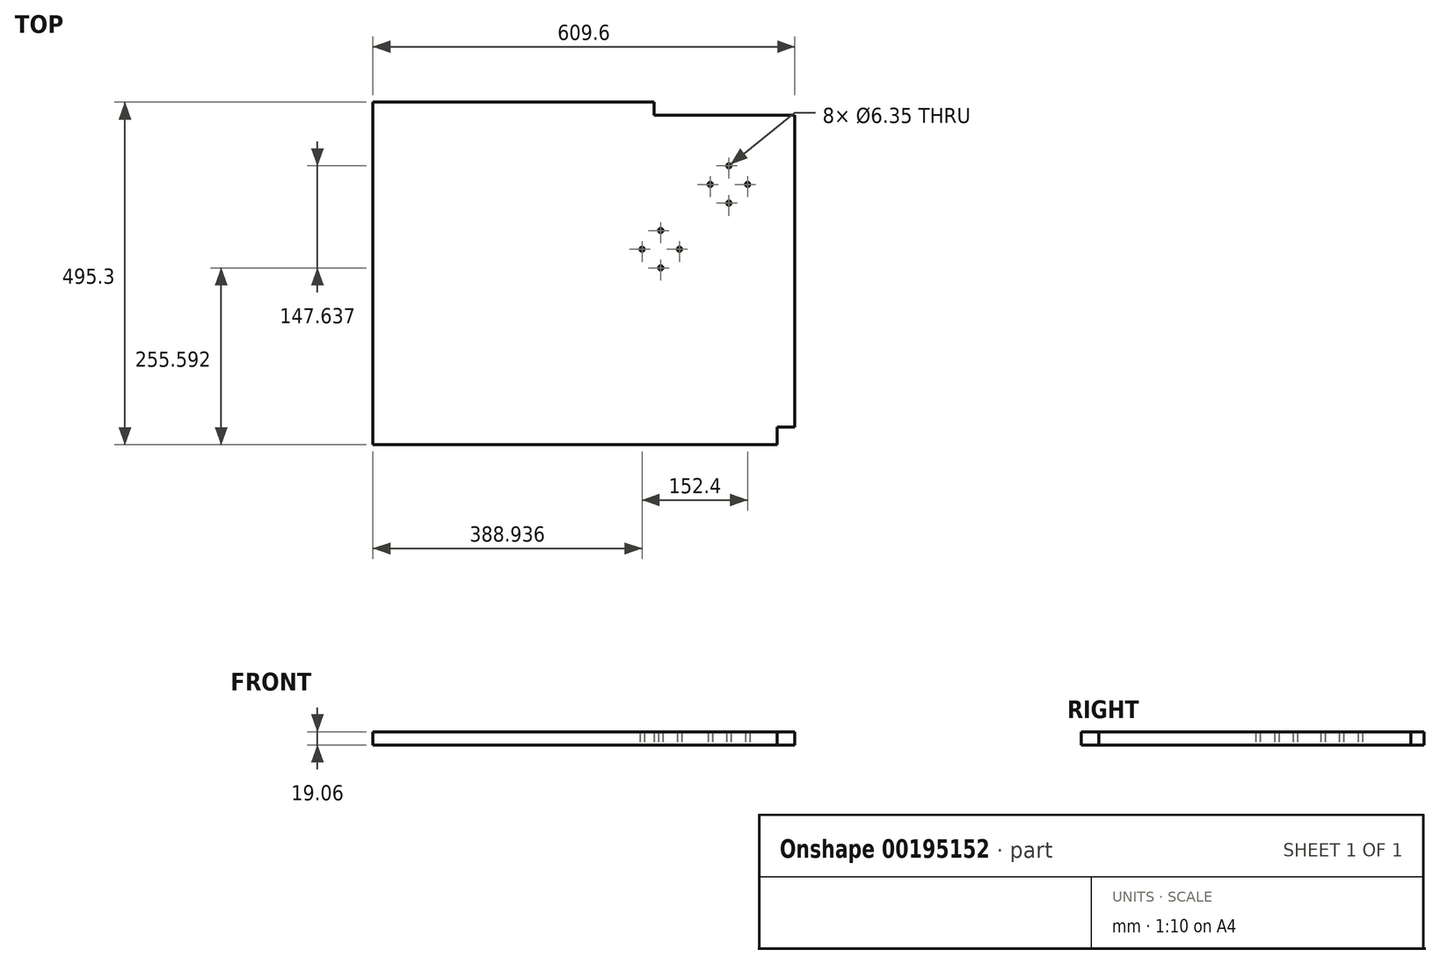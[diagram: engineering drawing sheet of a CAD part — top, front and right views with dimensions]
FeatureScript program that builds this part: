
annotation { "Feature Type Name" : "Feature", "Feature Type Description" : "" }
export const myFeature = defineFeature(function(context is Context, id is Id, definition is map)
    precondition{}
    {
        {
            var Q0;
            Q0=qCreatedBy(makeId("Top.planeOp"),FACE);
            var sketch = newSketch(context, id + "F0", { "sketchPlane" : qUnion([Q0])});
            skLineSegment(sketch, "E0", {"start": v(-565.53, 243.12) * mm, "end": v(-565.53, -252.18) * mm});
            skLineSegment(sketch, "E1", {"start": v(-565.53, -252.18) * mm, "end": v(18.67, -252.18) * mm});
            skLineSegment(sketch, "E2", {"start": v(18.67, -252.18) * mm, "end": v(18.67, -226.78) * mm});
            skLineSegment(sketch, "E3", {"start": v(18.67, -226.78) * mm, "end": v(44.07, -226.78) * mm});
            skLineSegment(sketch, "E4", {"start": v(44.07, -226.78) * mm, "end": v(44.07, 224.07) * mm});
            skLineSegment(sketch, "E5", {"start": v(44.07, 224.07) * mm, "end": v(-159.13, 224.07) * mm});
            skLineSegment(sketch, "E6", {"start": v(-159.13, 224.07) * mm, "end": v(-159.13, 243.12) * mm});
            skLineSegment(sketch, "E7", {"start": v(-159.13, 243.12) * mm, "end": v(-565.53, 243.12) * mm});
            skLineSegment(sketch, "E8", {"start": v(-418.3, -252.18) * mm, "end": v(-418.3, 30.4) * mm, "construction": true});
            skLineSegment(sketch, "E9", {"start": v(-273.43, -252.18) * mm, "end": v(-273.43, 124.06) * mm, "construction": true});
            skLineSegment(sketch, "E10", {"start": v(-273.43, 124.06) * mm, "end": v(44.07, 124.06) * mm, "construction": true});
            skLineSegment(sketch, "E11", {"start": v(-418.3, 30.4) * mm, "end": v(44.07, 30.4) * mm, "construction": true});
            skLineSegment(sketch, "E12", {"start": v(44.07, 178.98) * mm, "end": v(-51.18, 178.98) * mm, "construction": true});
            skLineSegment(sketch, "E13", {"start": v(-51.18, 178.98) * mm, "end": v(-51.18, -252.18) * mm, "construction": true});
            skLineSegment(sketch, "E14", {"start": v(44.07, 204.94) * mm, "end": v(-149.6, 204.94) * mm, "construction": true});
            skLineSegment(sketch, "E15", {"start": v(-149.6, 204.94) * mm, "end": v(-149.6, -252.18) * mm, "construction": true});
            skPoint(sketch, "E16", {"position": v(-149.6, 30.4) * mm});
            skPoint(sketch, "E17", {"position": v(-51.18, 124.06) * mm});
            skCircle(sketch, "E18", {"center": v(-149.6, 30.4) * mm, "radius": 26.99 * mm, "construction": true});
            skCircle(sketch, "E19", {"center": v(-51.18, 124.06) * mm, "radius": 26.99 * mm, "construction": true});
            skPoint(sketch, "E20", {"position": v(-149.6, 3.41) * mm});
            skPoint(sketch, "E21", {"position": v(-51.18, 97.07) * mm});
            skPoint(sketch, "E22", {"position": v(-24.2, 124.06) * mm});
            skPoint(sketch, "E23", {"position": v(-51.18, 151.05) * mm});
            skPoint(sketch, "E24", {"position": v(-78.17, 124.06) * mm});
            skPoint(sketch, "E25", {"position": v(-149.6, 57.39) * mm});
            skPoint(sketch, "E26", {"position": v(-176.6, 30.4) * mm});
            skPoint(sketch, "E27", {"position": v(-122.62, 30.4) * mm});
            skCircle(sketch, "E28", {"center": v(-149.6, 57.39) * mm, "radius": 3.18 * mm});
            skCircle(sketch, "E29", {"center": v(-176.6, 30.4) * mm, "radius": 3.18 * mm});
            skCircle(sketch, "E30", {"center": v(-149.6, 3.41) * mm, "radius": 3.18 * mm});
            skCircle(sketch, "E31", {"center": v(-122.62, 30.4) * mm, "radius": 3.18 * mm});
            skCircle(sketch, "E32", {"center": v(-78.17, 124.06) * mm, "radius": 3.18 * mm});
            skCircle(sketch, "E33", {"center": v(-51.18, 97.07) * mm, "radius": 3.18 * mm});
            skCircle(sketch, "E34", {"center": v(-24.2, 124.06) * mm, "radius": 3.18 * mm});
            skCircle(sketch, "E35", {"center": v(-51.18, 151.05) * mm, "radius": 3.18 * mm});
            skSolve(sketch);
        }
        {
            var Q0;
            Q0 = qSketchRegion(id + "F0", true);
            extrude(context, id + "F1", {"entities" : qUnion([Q0]), "endBound" : BoundingType.SYMMETRIC, "depth" : 19.05 * mm});
        }
    });
